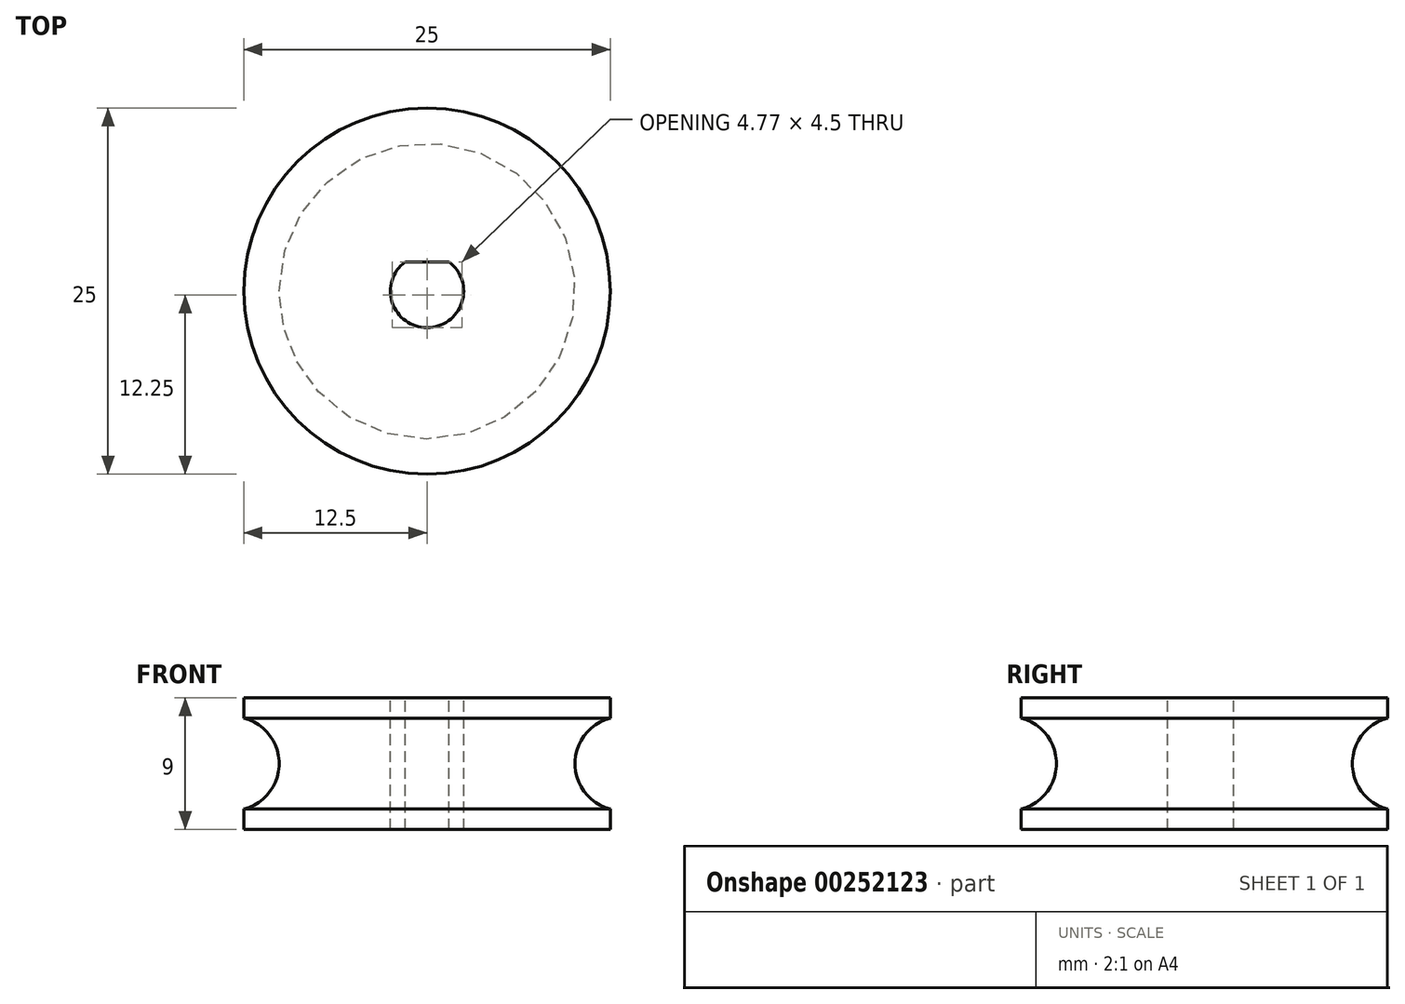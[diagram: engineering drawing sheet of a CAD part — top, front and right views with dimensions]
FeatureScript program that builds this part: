
annotation { "Feature Type Name" : "Feature", "Feature Type Description" : "" }
export const myFeature = defineFeature(function(context is Context, id is Id, definition is map)
    precondition{}
    {
        {
            var Q0;
            Q0=qCreatedBy(makeId("Front.planeOp"),FACE);
            var sketch = newSketch(context, id + "F0", { "sketchPlane" : qUnion([Q0])});
            skLineSegment(sketch, "E0", {"start": v(0, 0) * mm, "end": v(-12.5, 0) * mm});
            skLineSegment(sketch, "E1", {"start": v(-12.5, 0) * mm, "end": v(-12.5, 1.4) * mm});
            skLineSegment(sketch, "E2", {"start": v(0, 4.5) * mm, "end": v(-18.74, 4.5) * mm, "construction": true});
            skLineSegment(sketch, "E3.MirrorCS", {"start": v(-12.5, 9) * mm, "end": v(-12.5, 7.6) * mm});
            skLineSegment(sketch, "E4.MirrorCS", {"start": v(0, 9) * mm, "end": v(-12.5, 9) * mm});
            skArc(sketch, "E5", {"start": v(-12.5, 1.4) * mm, "mid": v(-10.1, 4.5) * mm, "end": v(-12.5, 7.6) * mm});
            skLineSegment(sketch, "E6", {"start": v(0, 0) * mm, "end": v(0, 9) * mm});
            skLineSegment(sketch, "E7", {"start": v(-10.1, 9) * mm, "end": v(-10.1, 0) * mm, "construction": true});
            skSolve(sketch);
        }
        {
            var Q0;
            Q0 = qSketchRegion(id + "F0", true);
            var Q1;
            Q1=sQuery(id+"F0.wireOp",EDGE,"E6");
            revolve(context, id + "F1", {"entities" : qUnion([Q0]), "axis" : qUnion([Q1]), "revolveType" : RevolveType.FULL});
        }
        {
            var Q0;
            Q0=makeQuery(id+"F1.opRevolve","SWEPT_FACE",FACE,{"disambiguationData":[OSD([sQuery(id+"F0.wireOp",EDGE,"E4.MirrorCS")])]});
            var sketch = newSketch(context, id + "F2", { "sketchPlane" : qUnion([Q0])});
            skArc(sketch, "E8", {"start": v(-1.5, 2) * mm, "mid": v(0, -2.5) * mm, "end": v(1.5, 2) * mm});
            skLineSegment(sketch, "E9", {"start": v(-1.5, 2) * mm, "end": v(1.5, 2) * mm});
            skSolve(sketch);
        }
        {
            var Q0;
            Q0 = qSketchRegion(id + "F2", true);
            extrude(context, id + "F3", {"entities" : qUnion([Q0]), "operationType" : NewBodyOperationType.REMOVE, "endBound" : BoundingType.THROUGH_ALL, "oppositeDirection" : true, "depth" : 25 * mm});
        }
    });
